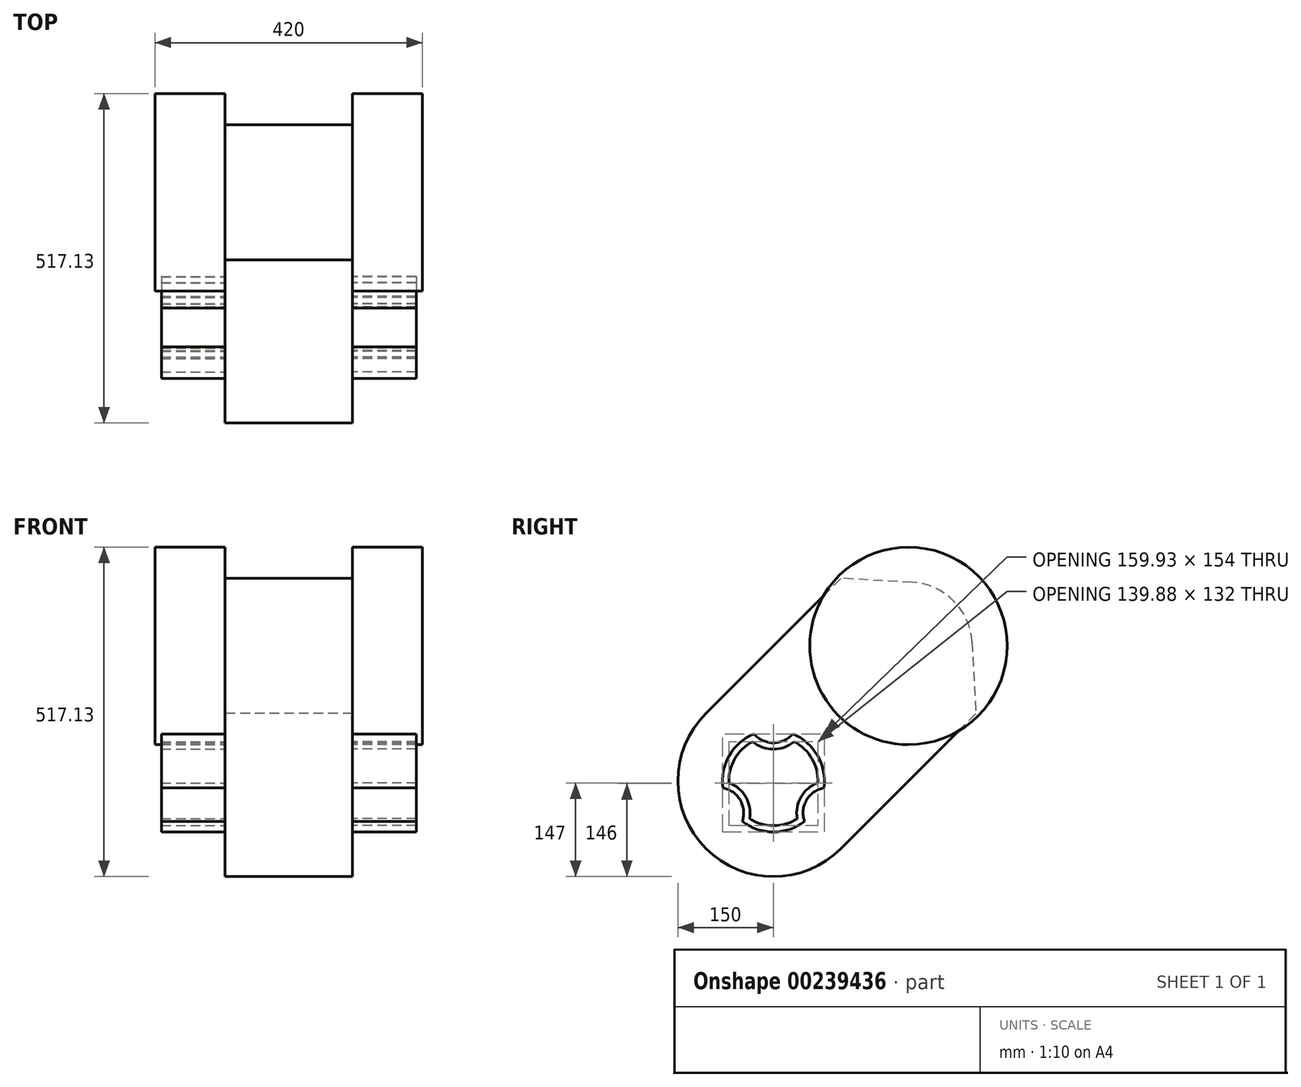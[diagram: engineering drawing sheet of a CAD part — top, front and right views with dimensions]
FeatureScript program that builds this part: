
annotation { "Feature Type Name" : "Feature", "Feature Type Description" : "" }
export const myFeature = defineFeature(function(context is Context, id is Id, definition is map)
    precondition{}
    {
        {
            var Q0;
            Q0=qCreatedBy(makeId("Right.planeOp"),FACE);
            var sketch = newSketch(context, id + "F0", { "sketchPlane" : qUnion([Q0])});
            skLineSegment(sketch, "E0", {"start": v(-106.07, 106.07) * mm, "end": v(106.07, 318.2) * mm});
            skLineSegment(sketch, "E1", {"start": v(106.07, -106.07) * mm, "end": v(318.2, 106.07) * mm});
            skLineSegment(sketch, "E2", {"start": v(0, 0) * mm, "end": v(212.13, 212.13) * mm, "construction": true});
            skArc(sketch, "E3", {"start": v(-106.07, 106.07) * mm, "mid": v(-106.07, -106.07) * mm, "end": v(106.07, -106.07) * mm});
            skArc(sketch, "E4", {"start": v(311.98, 217.7) * mm, "mid": v(282.84, 282.84) * mm, "end": v(217.7, 311.98) * mm});
            skLineSegment(sketch, "E5", {"start": v(217.7, 311.98) * mm, "end": v(106.07, 318.2) * mm});
            skLineSegment(sketch, "E6", {"start": v(311.98, 217.7) * mm, "end": v(318.2, 106.07) * mm});
            skLineSegment(sketch, "E7", {"start": v(0, 0) * mm, "end": v(310.83, 0) * mm, "construction": true});
            skCircle(sketch, "E8", {"center": v(212.13, 212.13) * mm, "radius": 155 * mm});
            skArc(sketch, "E9", {"start": v(-32.5, 62) * mm, "mid": v(-60.62, 35) * mm, "end": v(-69.94, -2.86) * mm});
            skArc(sketch, "E10", {"start": v(-32.5, 62) * mm, "mid": v(0, 50) * mm, "end": v(32.5, 62) * mm});
            skArc(sketch, "E11", {"start": v(69.94, -2.86) * mm, "mid": v(43.3, -25) * mm, "end": v(37.45, -59.14) * mm});
            skArc(sketch, "E12", {"start": v(-37.45, -59.14) * mm, "mid": v(-43.3, -25) * mm, "end": v(-69.94, -2.86) * mm});
            skArc(sketch, "E13", {"start": v(-30.4, 74) * mm, "mid": v(-69.28, 40) * mm, "end": v(-79.28, -10.68) * mm});
            skArc(sketch, "E14", {"start": v(-30.4, 74) * mm, "mid": v(0, 60) * mm, "end": v(30.4, 74) * mm});
            skArc(sketch, "E15", {"start": v(79.28, -10.68) * mm, "mid": v(51.96, -30) * mm, "end": v(48.89, -63.32) * mm});
            skArc(sketch, "E16", {"start": v(-48.89, -63.32) * mm, "mid": v(-51.96, -30) * mm, "end": v(-79.28, -10.68) * mm});
            skLineSegment(sketch, "E17", {"start": v(0, 100) * mm, "end": v(0, 0) * mm, "construction": true});
            skLineSegment(sketch, "E18", {"start": v(0, 0) * mm, "end": v(-86.6, -50) * mm, "construction": true});
            skLineSegment(sketch, "E19", {"start": v(0, 0) * mm, "end": v(86.6, -50) * mm, "construction": true});
            skArc(sketch, "E20.trimOffspring", {"start": v(69.94, -2.86) * mm, "mid": v(60.62, 35) * mm, "end": v(32.5, 62) * mm});
            skArc(sketch, "E21.trimOffspring", {"start": v(79.28, -10.68) * mm, "mid": v(69.28, 40) * mm, "end": v(30.4, 74) * mm});
            skArc(sketch, "E22.trimOffspring", {"start": v(-48.89, -63.32) * mm, "mid": v(0, -80) * mm, "end": v(48.89, -63.32) * mm});
            skArc(sketch, "E23.trimOffspring", {"start": v(-37.45, -59.14) * mm, "mid": v(0, -70) * mm, "end": v(37.45, -59.14) * mm});
            skSolve(sketch);
        }
        {
            var Q0;
            {var subQ0=sQuery(id+"F0.wireOp",EDGE,"E3");Q0=makeQuery(id+"F0.imprint","IMPRINT",FACE,{"disambiguationData":[TD([[makeQuery(id+"F0.imprint","IMPRINT",EDGE,{"derivedFrom":subQ0}),1.0]])]});}
            var Q1;
            Q1=makeQuery(id+"F0.imprint","IMPRINT",FACE,{"disambiguationData":[TD([[makeQuery(id+"F0.imprint","IMPRINT",EDGE,{"derivedFrom":sQuery(id+"F0.wireOp",EDGE,"E4")}),1.0]])]});
            var Q2;
            Q2=makeQuery(id+"F0.imprint","IMPRINT",FACE,{"disambiguationData":[TD([[makeQuery(id+"F0.imprint","IMPRINT",EDGE,{"derivedFrom":sQuery(id+"F0.wireOp",EDGE,"E9")}),-1.0]])]});
            var Q3;
            Q3=makeQuery(id+"F0.imprint","IMPRINT",FACE,{"disambiguationData":[TD([[makeQuery(id+"F0.imprint","IMPRINT",EDGE,{"derivedFrom":sQuery(id+"F0.wireOp",EDGE,"E9")}),1.0]])]});
            extrude(context, id + "F1", {"entities" : qUnion([Q0, Q1, Q2, Q3]), "depth" : 100 * mm});
        }
        {
            var Q0;
            Q0=makeQuery(id+"F0.imprint","IMPRINT",FACE,{"disambiguationData":[TD([[makeQuery(id+"F0.imprint","IMPRINT",EDGE,{"derivedFrom":sQuery(id+"F0.wireOp",EDGE,"E4")}),1.0]])]});
            var Q1;
            Q1=makeQuery(id+"F0.imprint","IMPRINT",FACE,{"disambiguationData":[TD([[makeQuery(id+"F0.imprint","IMPRINT",EDGE,{"derivedFrom":sQuery(id+"F0.wireOp",EDGE,"E4")}),-1.0]])]});
            var Q2;
            Q2=makeQuery(id+"F1.opExtrude","CAP_FACE",FACE,{"disambiguationData":[OSD([sQuery(id+"F0.wireOp",EDGE,"E0"),sQuery(id+"F0.wireOp",EDGE,"E1"),sQuery(id+"F0.wireOp",EDGE,"E3"),sQuery(id+"F0.wireOp",EDGE,"E4"),sQuery(id+"F0.wireOp",EDGE,"E5"),sQuery(id+"F0.wireOp",EDGE,"E6")])],"isStart":false});
            var Q3;
            Q3=makeQuery(id+"F1.opExtrude","CAP_FACE",FACE,{"disambiguationData":[OSD([sQuery(id+"F0.wireOp",EDGE,"E0"),sQuery(id+"F0.wireOp",EDGE,"E1"),sQuery(id+"F0.wireOp",EDGE,"E3"),sQuery(id+"F0.wireOp",EDGE,"E4"),sQuery(id+"F0.wireOp",EDGE,"E5"),sQuery(id+"F0.wireOp",EDGE,"E6")])],"isStart":false});
            extrude(context, id + "F2", {"entities" : qUnion([Q0, Q1]), "operationType" : NewBodyOperationType.ADD, "endBoundEntityFace" : qUnion([Q2]), "depth" : 210 * mm, "hasSecondDirection" : true, "secondDirectionBound" : SecondDirectionBoundingType.UP_TO_SURFACE, "secondDirectionOppositeDirection" : false, "secondDirectionBoundEntityFace" : qUnion([Q3]), "secondDirectionDepth" : 25 * mm});
        }
        {
            var Q0;
            Q0=makeQuery(id+"F0.imprint","IMPRINT",FACE,{"disambiguationData":[TD([[makeQuery(id+"F0.imprint","IMPRINT",EDGE,{"derivedFrom":sQuery(id+"F0.wireOp",EDGE,"E9")}),-1.0]])]});
            extrude(context, id + "F3", {"entities" : qUnion([Q0]), "operationType" : NewBodyOperationType.ADD, "depth" : 200 * mm});
        }
        {
            var Q0;
            Q0=makeQuery(id+"F1.opExtrude","SWEPT_BODY",BODY,{"disambiguationData":[OSD([sQuery(id+"F0.wireOp",EDGE,"E0"),sQuery(id+"F0.wireOp",EDGE,"E1"),sQuery(id+"F0.wireOp",EDGE,"E3"),sQuery(id+"F0.wireOp",EDGE,"E4"),sQuery(id+"F0.wireOp",EDGE,"E5"),sQuery(id+"F0.wireOp",EDGE,"E6")])]});
            var Q1;
            {var subQ0=sQuery(id+"F0.wireOp",EDGE,"E3");Q1=makeQuery(id+"F0.imprint","IMPRINT",FACE,{"disambiguationData":[TD([[makeQuery(id+"F0.imprint","IMPRINT",EDGE,{"derivedFrom":subQ0}),1.0]])]});}
            mirror(context, id + "F4", {"operationType" : NewBodyOperationType.ADD, "entities" : qUnion([Q0]), "mirrorPlane" : qUnion([Q1])});
        }
    });
